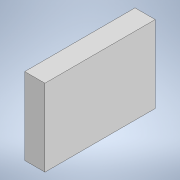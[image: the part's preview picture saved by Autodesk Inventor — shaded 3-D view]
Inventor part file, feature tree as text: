
AUTODESK INVENTOR PART (.ipt)
format: ipt  version: 2022 (Build 260153070, 153G)  size: 87,040 bytes
history: native  units: in
note: dims shown in document units (in); Inventor stores cm internally (conversion verified against a paired STEP export)
features: extrude x1, sketch x1
ambient origin geometry x8: Origin, YZ Plane, XZ Plane, XY Plane, X Axis, Y Axis, Z Axis, Center Point
bodies: Solid1 (feature_tree)
feature tree (2):
  extrude  "Extrusion1"  Depth=2.0949in
  sketch  "Sketch1"  dims[d0=3.0in d1=2.0949in d2=0.55in d3=0.0in]
